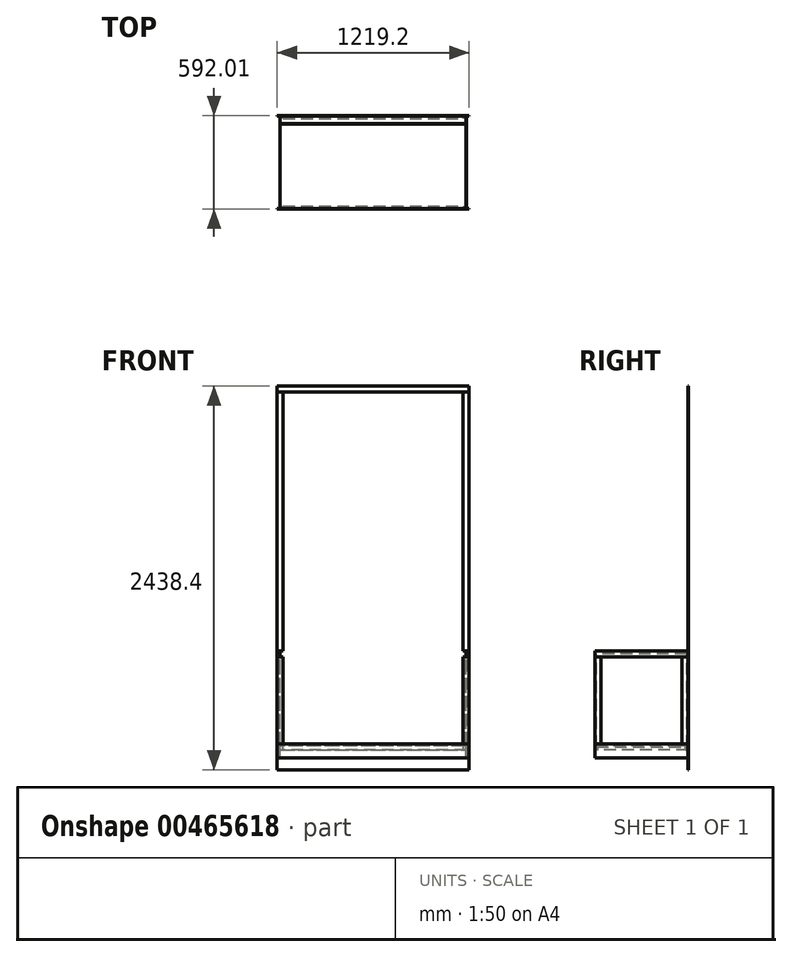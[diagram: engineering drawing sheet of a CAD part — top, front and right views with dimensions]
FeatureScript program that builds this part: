
annotation { "Feature Type Name" : "Feature", "Feature Type Description" : "" }
export const myFeature = defineFeature(function(context is Context, id is Id, definition is map)
    precondition{}
    {
        {
            assignVariable(context, id + "F0", {"name" : "TotalHeight", "anyValue" : 24});
        }
        {
            assignVariable(context, id + "F1", {"name" : "x1", "anyValue" : 0.75});
        }
        {
            assignVariable(context, id + "F2", {"name" : "PlyThk", "anyValue" : 23 / 32});
        }
        {
            var Q0;
            Q0=qCreatedBy(makeId("Top.planeOp"),FACE);
            var sketch = newSketch(context, id + "F3", { "sketchPlane" : qUnion([Q0])});
            skLineSegment(sketch, "E0.bottom", {"start": v(609.6, 295.28) * mm, "end": v(-609.6, 295.27) * mm, "construction": true});
            skLineSegment(sketch, "E0.top", {"start": v(609.6, -314.32) * mm, "end": v(-609.6, -314.33) * mm, "construction": true});
            skLineSegment(sketch, "E0.left", {"start": v(609.6, 295.28) * mm, "end": v(609.6, -314.32) * mm, "construction": true});
            skLineSegment(sketch, "E0.right", {"start": v(-609.6, 295.27) * mm, "end": v(-609.6, -314.33) * mm, "construction": true});
            skPoint(sketch, "E0.middle", {"position": v(0, 0) * mm});
            skLineSegment(sketch, "E1.bottom", {"start": v(590.55, 295.28) * mm, "end": v(-590.55, 295.27) * mm});
            skLineSegment(sketch, "E1.top", {"start": v(590.55, -295.27) * mm, "end": v(-590.55, -295.28) * mm});
            skLineSegment(sketch, "E1.left", {"start": v(590.55, 295.28) * mm, "end": v(590.55, -295.27) * mm});
            skLineSegment(sketch, "E1.right", {"start": v(-590.55, 295.27) * mm, "end": v(-590.55, -295.28) * mm});
            skSolve(sketch);
        }
        {
            var Q0;
            Q0=makeQuery(id+"F3.imprint","IMPRINT",FACE,{"disambiguationData":[TD([[makeQuery(id+"F3.imprint","IMPRINT",EDGE,{"derivedFrom":sQuery(id+"F3.wireOp",EDGE,"E1.bottom")}),1.0]])]});
            extrude(context, id + "F4", {"entities" : qUnion([Q0]), "depth" : (getVariable(context, 'PlyThk')) * mm});
        }
        {
            var Q0;
            Q0=makeQuery(id+"F4.opExtrude","CAP_FACE",FACE,{"disambiguationData":[OSD([sQuery(id+"F3.wireOp",EDGE,"E1.bottom"),sQuery(id+"F3.wireOp",EDGE,"E1.top"),sQuery(id+"F3.wireOp",EDGE,"E1.left"),sQuery(id+"F3.wireOp",EDGE,"E1.right")])],"isStart":true});
            cPlane(context, id + "F5", {"entities" : qUnion([Q0]), "cplaneType" : CPlaneType.OFFSET, "offset" : (getVariable(context, 'TotalHeight')) * mm, "oppositeDirection" : true, "width" : 152.4 * mm, "height" : 152.4 * mm});
        }
        {
            var Q0;
            Q0=qCreatedBy(id+"F5.planeOp",FACE);
            var sketch = newSketch(context, id + "F6", { "sketchPlane" : qUnion([Q0])});
            skLineSegment(sketch, "E2.0", {"start": v(590.55, 295.27) * mm, "end": v(-590.55, 295.28) * mm});
            skLineSegment(sketch, "E3", {"start": v(-590.55, 295.28) * mm, "end": v(-590.55, 286.15) * mm});
            skLineSegment(sketch, "E4", {"start": v(-590.55, 286.15) * mm, "end": v(-572.3, 286.15) * mm});
            skLineSegment(sketch, "E5", {"start": v(-572.3, 286.15) * mm, "end": v(-572.3, 277.02) * mm});
            skLineSegment(sketch, "E6.MirrorCS", {"start": v(590.55, 295.28) * mm, "end": v(590.55, 286.15) * mm});
            skLineSegment(sketch, "E7.MirrorCS", {"start": v(572.3, 286.15) * mm, "end": v(572.3, 277.02) * mm});
            skLineSegment(sketch, "E8.MirrorCS", {"start": v(590.55, 286.15) * mm, "end": v(572.3, 286.15) * mm});
            skLineSegment(sketch, "E9", {"start": v(572.3, 277.02) * mm, "end": v(-572.3, 277.02) * mm});
            skLineSegment(sketch, "E10.MirrorCS", {"start": v(-590.55, -295.28) * mm, "end": v(-590.55, -286.15) * mm});
            skLineSegment(sketch, "E11.MirrorCS", {"start": v(-590.55, -286.15) * mm, "end": v(-572.3, -286.15) * mm});
            skLineSegment(sketch, "E12.MirrorCS", {"start": v(-572.3, -286.15) * mm, "end": v(-572.3, -277.02) * mm});
            skLineSegment(sketch, "E13.MirrorCS", {"start": v(590.55, -295.28) * mm, "end": v(590.55, -286.15) * mm});
            skLineSegment(sketch, "E14.MirrorCS", {"start": v(572.3, -286.15) * mm, "end": v(572.3, -277.02) * mm});
            skLineSegment(sketch, "E15.MirrorCS", {"start": v(590.55, -286.15) * mm, "end": v(572.3, -286.15) * mm});
            skLineSegment(sketch, "E16.MirrorCS", {"start": v(590.55, -295.27) * mm, "end": v(-590.55, -295.27) * mm});
            skLineSegment(sketch, "E17.MirrorCS", {"start": v(572.3, -277.02) * mm, "end": v(-572.3, -277.02) * mm});
            skSolve(sketch);
        }
        {
            var Q0;
            Q0=makeQuery(id+"F6.imprint","IMPRINT",FACE,{"disambiguationData":[TD([[makeQuery(id+"F6.imprint","IMPRINT",EDGE,{"derivedFrom":sQuery(id+"F6.wireOp",EDGE,"E2.0")}),1.0]])]});
            var Q1;
            Q1=makeQuery(id+"F6.imprint","IMPRINT",FACE,{"disambiguationData":[TD([[makeQuery(id+"F6.imprint","IMPRINT",EDGE,{"derivedFrom":sQuery(id+"F6.wireOp",EDGE,"E10.MirrorCS")}),-1.0]])]});
            var Q2;
            Q2=makeQuery(id+"F4.opExtrude","CAP_FACE",FACE,{"disambiguationData":[OSD([sQuery(id+"F3.wireOp",EDGE,"E1.bottom"),sQuery(id+"F3.wireOp",EDGE,"E1.top"),sQuery(id+"F3.wireOp",EDGE,"E1.left"),sQuery(id+"F3.wireOp",EDGE,"E1.right")])],"isStart":false});
            extrude(context, id + "F7", {"entities" : qUnion([Q0, Q1]), "endBound" : BoundingType.UP_TO_SURFACE, "endBoundEntityFace" : qUnion([Q2]), "depth" : 25.4 * mm});
        }
        {
            var Q0;
            Q0=makeQuery(id+"F7.opExtrude","SWEPT_FACE",FACE,{"disambiguationData":[OSD([sQuery(id+"F6.wireOp",EDGE,"E6.MirrorCS")])]});
            var sketch = newSketch(context, id + "F8", { "sketchPlane" : qUnion([Q0])});
            skLineSegment(sketch, "E18.0", {"start": v(-286.15, 18.26) * mm, "end": v(-286.15, 609.6) * mm});
            skLineSegment(sketch, "E19.0", {"start": v(286.15, 18.26) * mm, "end": v(286.15, 609.6) * mm});
            skLineSegment(sketch, "E20", {"start": v(286.15, 609.6) * mm, "end": v(-286.15, 609.6) * mm});
            skLineSegment(sketch, "E21", {"start": v(-286.15, 18.26) * mm, "end": v(286.15, 18.26) * mm});
            skSolve(sketch);
        }
        {
            var Q0;
            Q0 = qSketchRegion(id + "F8", true);
            extrude(context, id + "F9", {"entities" : qUnion([Q0]), "oppositeDirection" : true, "depth" : (getVariable(context, 'PlyThk')) * mm});
        }
        {
            var Q0;
            Q0=makeQuery(id+"F9.opExtrude","SWEPT_BODY",BODY,{"disambiguationData":[OSD([sQuery(id+"F8.wireOp",EDGE,"E18.0"),sQuery(id+"F8.wireOp",EDGE,"E19.0"),sQuery(id+"F8.wireOp",EDGE,"E20"),sQuery(id+"F8.wireOp",EDGE,"E21")])]});
            var Q1;
            Q1=qCreatedBy(makeId("Right.planeOp"),FACE);
            mirror(context, id + "F10", {"entities" : qUnion([Q0]), "mirrorPlane" : qUnion([Q1])});
        }
        {
            var Q0;
            Q0=makeQuery(id+"F10.opPattern","COPY",FACE,{"derivedFrom":makeQuery(id+"F9.opExtrude","CAP_FACE",FACE,{"disambiguationData":[OSD([sQuery(id+"F8.wireOp",EDGE,"E18.0"),sQuery(id+"F8.wireOp",EDGE,"E19.0"),sQuery(id+"F8.wireOp",EDGE,"E20"),sQuery(id+"F8.wireOp",EDGE,"E21")])],"isStart":true}),"instanceName":"1"});
            var sketch = newSketch(context, id + "F11", { "sketchPlane" : qUnion([Q0])});
            skPoint(sketch, "E22.0", {"position": v(290.71, 609.6) * mm});
            skLineSegment(sketch, "E23.0", {"start": v(295.27, 609.6) * mm, "end": v(286.15, 609.6) * mm});
            skLineSegment(sketch, "E24.0", {"start": v(-295.27, 609.6) * mm, "end": v(-286.15, 609.6) * mm});
            skLineSegment(sketch, "E25.0", {"start": v(-295.28, 18.26) * mm, "end": v(-295.28, 609.6) * mm});
            skLineSegment(sketch, "E26.0", {"start": v(295.28, 18.26) * mm, "end": v(295.28, 609.6) * mm});
            skLineSegment(sketch, "E27", {"start": v(295.28, 589.76) * mm, "end": v(-295.28, 589.76) * mm});
            skLineSegment(sketch, "E28.bottom", {"start": v(-295.27, 38.1) * mm, "end": v(295.27, 38.1) * mm});
            skLineSegment(sketch, "E28.top", {"start": v(-295.27, -50.8) * mm, "end": v(295.27, -50.8) * mm});
            skLineSegment(sketch, "E28.left", {"start": v(-295.27, 38.1) * mm, "end": v(-295.27, -50.8) * mm});
            skLineSegment(sketch, "E28.right", {"start": v(295.27, 38.1) * mm, "end": v(295.27, -50.8) * mm});
            skLineSegment(sketch, "E29", {"start": v(-257.17, 589.76) * mm, "end": v(-257.17, 38.1) * mm});
            skLineSegment(sketch, "E30", {"start": v(257.17, 589.76) * mm, "end": v(257.18, 38.1) * mm});
            skLineSegment(sketch, "E31", {"start": v(-295.27, 609.6) * mm, "end": v(-295.27, 627.86) * mm});
            skLineSegment(sketch, "E32", {"start": v(-295.28, 627.86) * mm, "end": v(295.28, 627.86) * mm});
            skLineSegment(sketch, "E33", {"start": v(295.27, 627.86) * mm, "end": v(295.27, 609.6) * mm});
            skSolve(sketch);
        }
        {
            var Q0;
            {var subQ0=sQuery(id+"F11.wireOp",EDGE,"E23.0");Q0=makeQuery(id+"F11.imprint","IMPRINT",FACE,{"disambiguationData":[TD([[makeQuery(id+"F11.imprint","IMPRINT",EDGE,{"derivedFrom":subQ0}),1.0]])]});}
            var Q1;
            {var subQ0=sQuery(id+"F11.wireOp",EDGE,"E24.0");Q1=makeQuery(id+"F11.imprint","IMPRINT",FACE,{"disambiguationData":[TD([[makeQuery(id+"F11.imprint","IMPRINT",EDGE,{"derivedFrom":subQ0}),-1.0]])]});}
            var Q2;
            {var subQ3=sQuery(id+"F11.wireOp",EDGE,"E28.top");Q2=makeQuery(id+"F11.imprint","IMPRINT",FACE,{"disambiguationData":[TD([[makeQuery(id+"F11.imprint","IMPRINT",EDGE,{"derivedFrom":subQ3}),1.0]])]});}
            var Q3;
            {var subQ0=makeQuery(id+"F10.opPattern","COPY",EDGE,{"derivedFrom":makeQuery(id+"F9.opExtrude","CAP_EDGE",EDGE,{"disambiguationData":[OSD([sQuery(id+"F8.wireOp",EDGE,"E21")])],"isStart":true}),"instanceName":"1"});Q3=makeQuery(id+"F11.imprint","IMPRINT",FACE,{"disambiguationData":[TD([[makeQuery(id+"F11.imprint","IMPRINT",EDGE,{"derivedFrom":subQ0}),-1.0]])]});}
            var Q4;
            {var subQ7=sQuery(id+"F11.wireOp",EDGE,"92d246fa-3d92-4376-9fad-c65cf3820cd6.0");Q4=makeQuery(id+"F11.imprint","IMPRINT",FACE,{"disambiguationData":[TD([[makeQuery(id+"F11.imprint","IMPRINT",EDGE,{"derivedFrom":subQ7}),-1.0]])]});}
            var Q5;
            Q5=makeQuery(id+"F11.imprint","IMPRINT",FACE,{"disambiguationData":[TD([[makeQuery(id+"F11.imprint","IMPRINT",EDGE,{"derivedFrom":sQuery(id+"F11.wireOp",EDGE,"E23.0")}),-1.0]])]});
            var Q6;
            {var subQ0=makeQuery(id+"F10.opPattern","COPY",EDGE,{"derivedFrom":makeQuery(id+"F9.opExtrude","CAP_EDGE",EDGE,{"disambiguationData":[OSD([sQuery(id+"F8.wireOp",EDGE,"E20")])],"isStart":true}),"instanceName":"1"});Q6=makeQuery(id+"F11.imprint","IMPRINT",FACE,{"disambiguationData":[TD([[makeQuery(id+"F11.imprint","IMPRINT",EDGE,{"derivedFrom":subQ0}),-1.0]])]});}
            extrude(context, id + "F12", {"entities" : qUnion([Q0, Q1, Q2, Q3, Q4, Q5, Q6]), "depth" : (getVariable(context, 'x1')) * mm});
        }
        {
            var Q0;
            {var subQ0=sQuery(id+"F11.wireOp",EDGE,"E29");Q0=makeQuery(id+"F11.imprint","IMPRINT",FACE,{"disambiguationData":[TD([[makeQuery(id+"F11.imprint","IMPRINT",EDGE,{"derivedFrom":subQ0}),-1.0]])]});}
            var Q1;
            {var subQ1=sQuery(id+"F11.wireOp",EDGE,"E25.0");var subQ3=sQuery(id+"F11.wireOp",EDGE,"E27");var subQ4=makeQuery(id+"F11.imprint","INTERSECT",VERTEX,{"derivedFrom":[subQ1,subQ3]});Q1=makeQuery(id+"F11.imprint","IMPRINT",FACE,{"disambiguationData":[TD([[makeQuery(id+"F11.imprint","IMPRINT",EDGE,{"disambiguationData":[TD([[subQ4,1.0]])],"derivedFrom":subQ3}),1.0]])]});}
            var Q2;
            {var subQ0=sQuery(id+"F11.wireOp",EDGE,"E30");Q2=makeQuery(id+"F11.imprint","IMPRINT",FACE,{"disambiguationData":[TD([[makeQuery(id+"F11.imprint","IMPRINT",EDGE,{"derivedFrom":subQ0}),1.0]])]});}
            var Q3;
            {var subQ1=sQuery(id+"F11.wireOp",EDGE,"E26.0");var subQ3=sQuery(id+"F11.wireOp",EDGE,"E27");var subQ4=makeQuery(id+"F11.imprint","INTERSECT",VERTEX,{"derivedFrom":[subQ1,subQ3]});Q3=makeQuery(id+"F11.imprint","IMPRINT",FACE,{"disambiguationData":[TD([[makeQuery(id+"F11.imprint","IMPRINT",EDGE,{"disambiguationData":[TD([[subQ4,-1.0]])],"derivedFrom":subQ3}),1.0]])]});}
            extrude(context, id + "F13", {"entities" : qUnion([Q0, Q1, Q2, Q3]), "depth" : (getVariable(context, 'x1')) * mm});
        }
        {
            var Q0;
            Q0=makeQuery(id+"F12.opExtrude","SWEPT_BODY",BODY,{"disambiguationData":[OSD([sQuery(id+"F11.wireOp",EDGE,"E28.bottom"),sQuery(id+"F11.wireOp",EDGE,"E28.top"),sQuery(id+"F11.wireOp",EDGE,"E28.left"),sQuery(id+"F11.wireOp",EDGE,"E28.right")])]});
            var Q1;
            Q1=makeQuery(id+"F13.opExtrude","SWEPT_BODY",BODY,{"disambiguationData":[OSD([sQuery(id+"F11.wireOp",EDGE,"E26.0"),sQuery(id+"F11.wireOp",EDGE,"E27"),sQuery(id+"F11.wireOp",EDGE,"E28.bottom"),sQuery(id+"F11.wireOp",EDGE,"E30")])]});
            var Q2;
            Q2=makeQuery(id+"F12.opExtrude","SWEPT_BODY",BODY,{"disambiguationData":[OSD([sQuery(id+"F11.wireOp",EDGE,"92d246fa-3d92-4376-9fad-c65cf3820cd6.0"),sQuery(id+"F11.wireOp",EDGE,"E23.0"),sQuery(id+"F11.wireOp",EDGE,"E24.0"),sQuery(id+"F11.wireOp",EDGE,"E25.0"),sQuery(id+"F11.wireOp",EDGE,"E26.0"),sQuery(id+"F11.wireOp",EDGE,"E27")])]});
            var Q3;
            Q3=makeQuery(id+"F13.opExtrude","SWEPT_BODY",BODY,{"disambiguationData":[OSD([sQuery(id+"F11.wireOp",EDGE,"E25.0"),sQuery(id+"F11.wireOp",EDGE,"E27"),sQuery(id+"F11.wireOp",EDGE,"E28.bottom"),sQuery(id+"F11.wireOp",EDGE,"E29")])]});
            var Q4;
            Q4=qCreatedBy(makeId("Right.planeOp"),FACE);
            mirror(context, id + "F14", {"entities" : qUnion([Q0, Q1, Q2, Q3]), "mirrorPlane" : qUnion([Q4])});
        }
        {
            var Q0;
            Q0=makeQuery(id+"F7.opExtrude","SWEPT_FACE",FACE,{"disambiguationData":[OSD([sQuery(id+"F6.wireOp",EDGE,"E2.0")])]});
            var sketch = newSketch(context, id + "F15", { "sketchPlane" : qUnion([Q0])});
            skLineSegment(sketch, "E34.0", {"start": v(-609.6, 38.1) * mm, "end": v(-609.6, 589.76) * mm});
            skLineSegment(sketch, "E35.0", {"start": v(-609.6, 589.76) * mm, "end": v(-609.6, 589.76) * mm});
            skLineSegment(sketch, "E36.0", {"start": v(-609.6, 38.1) * mm, "end": v(-609.6, -50.8) * mm});
            skLineSegment(sketch, "E37.0", {"start": v(609.6, 38.1) * mm, "end": v(609.6, -50.8) * mm});
            skLineSegment(sketch, "E38", {"start": v(609.6, -50.8) * mm, "end": v(-609.6, -50.8) * mm});
            skLineSegment(sketch, "E39", {"start": v(-609.6, 38.1) * mm, "end": v(609.6, 38.1) * mm});
            skLineSegment(sketch, "E40", {"start": v(-609.6, 589.76) * mm, "end": v(609.6, 589.76) * mm});
            skLineSegment(sketch, "E41.0", {"start": v(609.6, 589.76) * mm, "end": v(609.6, 589.76) * mm});
            skLineSegment(sketch, "E42.0.0", {"start": v(590.55, 589.76) * mm, "end": v(590.55, 589.76) * mm});
            skLineSegment(sketch, "E42.0.1", {"start": v(590.55, 589.76) * mm, "end": v(609.6, 589.76) * mm});
            skLineSegment(sketch, "E42.0.3", {"start": v(590.55, 589.76) * mm, "end": v(609.6, 589.76) * mm});
            skLineSegment(sketch, "E43.0.0", {"start": v(-590.55, 589.76) * mm, "end": v(-590.55, 589.76) * mm});
            skLineSegment(sketch, "E43.0.1", {"start": v(-609.6, 589.76) * mm, "end": v(-590.55, 589.76) * mm});
            skLineSegment(sketch, "E43.0.3", {"start": v(-609.6, 589.76) * mm, "end": v(-590.55, 589.76) * mm});
            skLineSegment(sketch, "E44", {"start": v(-571.5, 589.76) * mm, "end": v(-571.5, 38.1) * mm});
            skLineSegment(sketch, "E45", {"start": v(571.5, 589.76) * mm, "end": v(571.5, 38.1) * mm});
            skLineSegment(sketch, "E46", {"start": v(609.6, 589.76) * mm, "end": v(609.6, 38.1) * mm});
            skLineSegment(sketch, "E47", {"start": v(590.55, 627.86) * mm, "end": v(-590.55, 627.86) * mm});
            skLineSegment(sketch, "E48", {"start": v(609.6, 589.76) * mm, "end": v(609.6, 627.86) * mm});
            skLineSegment(sketch, "E49", {"start": v(609.6, 627.86) * mm, "end": v(590.55, 627.86) * mm});
            skLineSegment(sketch, "E50", {"start": v(-609.6, 589.76) * mm, "end": v(-609.6, 627.86) * mm});
            skLineSegment(sketch, "E51", {"start": v(-609.6, 627.86) * mm, "end": v(-590.55, 627.86) * mm});
            skSolve(sketch);
        }
        {
            var Q0;
            {var subQ1=sQuery(id+"F15.wireOp",EDGE,"E36.0");Q0=makeQuery(id+"F15.imprint","IMPRINT",FACE,{"disambiguationData":[TD([[makeQuery(id+"F15.imprint","IMPRINT",EDGE,{"derivedFrom":subQ1}),1.0]])]});}
            var Q1;
            {var subQ2=sQuery(id+"F15.wireOp",EDGE,"E39");var subQ6=makeQuery(id+"F15.imprint","INTERSECT",VERTEX,{"derivedFrom":[subQ2,sQuery(id+"F15.wireOp",EDGE,"E44")]});Q1=makeQuery(id+"F15.imprint","IMPRINT",FACE,{"disambiguationData":[TD([[makeQuery(id+"F15.imprint","IMPRINT",EDGE,{"disambiguationData":[TD([[subQ6,-1.0]])],"derivedFrom":subQ2}),-1.0]])]});}
            var Q2;
            {var subQ0=sQuery(id+"F15.wireOp",EDGE,"E42.0.0");Q2=makeQuery(id+"F15.imprint","IMPRINT",FACE,{"disambiguationData":[TD([[makeQuery(id+"F15.imprint","IMPRINT",EDGE,{"derivedFrom":subQ0}),1.0]])]});}
            var Q3;
            Q3=makeQuery(id+"F15.imprint","IMPRINT",FACE,{"disambiguationData":[TD([[makeQuery(id+"F15.imprint","IMPRINT",EDGE,{"derivedFrom":sQuery(id+"F15.wireOp",EDGE,"E43.0.0")}),1.0]])]});
            var Q4;
            Q4=makeQuery(id+"F15.imprint","IMPRINT",FACE,{"disambiguationData":[TD([[makeQuery(id+"F15.imprint","IMPRINT",EDGE,{"derivedFrom":sQuery(id+"F15.wireOp",EDGE,"E42.0.0")}),-1.0]])]});
            var Q5;
            {var subQ4=sQuery(id+"F15.wireOp",EDGE,"E42.0.3");Q5=makeQuery(id+"F15.imprint","IMPRINT",FACE,{"disambiguationData":[TD([[makeQuery(id+"F15.imprint","IMPRINT",EDGE,{"derivedFrom":subQ4}),1.0]])]});}
            var Q6;
            {var subQ0=sQuery(id+"F6.wireOp",EDGE,"E2.0");var subQ1=makeQuery(id+"F7.opExtrude","CAP_EDGE",EDGE,{"disambiguationData":[OSD([subQ0])],"isStart":true});Q6=makeQuery(id+"F15.imprint","IMPRINT",FACE,{"disambiguationData":[TD([[makeQuery(id+"F15.imprint","IMPRINT",EDGE,{"derivedFrom":subQ1}),1.0]])]});}
            extrude(context, id + "F16", {"entities" : qUnion([Q0, Q1, Q2, Q3, Q4, Q5, Q6]), "depth" : (getVariable(context, 'x1')) * mm});
        }
        {
            var Q0;
            {var subQ0=sQuery(id+"F15.wireOp",EDGE,"E44");Q0=makeQuery(id+"F15.imprint","IMPRINT",FACE,{"disambiguationData":[TD([[makeQuery(id+"F15.imprint","IMPRINT",EDGE,{"derivedFrom":subQ0}),-1.0]])]});}
            var Q1;
            {var subQ0=sQuery(id+"F15.wireOp",EDGE,"E34.0");Q1=makeQuery(id+"F15.imprint","IMPRINT",FACE,{"disambiguationData":[TD([[makeQuery(id+"F15.imprint","IMPRINT",EDGE,{"derivedFrom":subQ0}),-1.0]])]});}
            var Q2;
            {var subQ4=sQuery(id+"F15.wireOp",EDGE,"E42.0.1");Q2=makeQuery(id+"F15.imprint","IMPRINT",FACE,{"disambiguationData":[TD([[makeQuery(id+"F15.imprint","IMPRINT",EDGE,{"derivedFrom":subQ4}),-1.0]])]});}
            var Q3;
            {var subQ4=sQuery(id+"F15.wireOp",EDGE,"E42.0.3");Q3=makeQuery(id+"F15.imprint","IMPRINT",FACE,{"disambiguationData":[TD([[makeQuery(id+"F15.imprint","IMPRINT",EDGE,{"derivedFrom":subQ4}),-1.0]])]});}
            var Q4;
            {var subQ0=sQuery(id+"F15.wireOp",EDGE,"E45");Q4=makeQuery(id+"F15.imprint","IMPRINT",FACE,{"disambiguationData":[TD([[makeQuery(id+"F15.imprint","IMPRINT",EDGE,{"derivedFrom":subQ0}),1.0]])]});}
            extrude(context, id + "F17", {"entities" : qUnion([Q0, Q1, Q2, Q3, Q4]), "depth" : (getVariable(context, 'x1')) * mm});
        }
        {
            var Q0;
            Q0=qCreatedBy(id+"F5.planeOp",FACE);
            var sketch = newSketch(context, id + "F18", { "sketchPlane" : qUnion([Q0])});
            skLineSegment(sketch, "E52.0", {"start": v(590.55, -295.27) * mm, "end": v(-590.55, -295.27) * mm});
            skLineSegment(sketch, "E53.0", {"start": v(-609.6, 295.28) * mm, "end": v(609.6, 295.27) * mm});
            skLineSegment(sketch, "E54", {"start": v(590.55, -244.47) * mm, "end": v(-590.55, -244.47) * mm});
            skLineSegment(sketch, "E55", {"start": v(-590.55, -241.3) * mm, "end": v(590.55, -241.3) * mm});
            skLineSegment(sketch, "E56.0", {"start": v(-590.55, -295.27) * mm, "end": v(-590.55, 295.28) * mm});
            skLineSegment(sketch, "E57.0", {"start": v(590.55, -295.27) * mm, "end": v(590.55, 295.28) * mm});
            skLineSegment(sketch, "E58.0", {"start": v(-609.6, 314.33) * mm, "end": v(-609.6, 295.28) * mm, "construction": true});
            skSolve(sketch);
        }
        {
            var Q0;
            {var subQ3=sQuery(id+"F18.wireOp",EDGE,"E55");Q0=makeQuery(id+"F18.imprint","IMPRINT",FACE,{"disambiguationData":[TD([[makeQuery(id+"F18.imprint","IMPRINT",EDGE,{"derivedFrom":subQ3}),1.0]])]});}
            extrude(context, id + "F19", {"entities" : qUnion([Q0]), "oppositeDirection" : true, "depth" : (getVariable(context, 'PlyThk')) * mm});
        }
        {
            var Q0;
            {var subQ0=sQuery(id+"F18.wireOp",EDGE,"E52.0");Q0=makeQuery(id+"F18.imprint","IMPRINT",FACE,{"disambiguationData":[TD([[makeQuery(id+"F18.imprint","IMPRINT",EDGE,{"derivedFrom":subQ0}),-1.0]])]});}
            extrude(context, id + "F20", {"entities" : qUnion([Q0]), "oppositeDirection" : true, "depth" : (getVariable(context, 'PlyThk')) * mm});
        }
        {
            var Q0;
            Q0=makeQuery(id+"F7.opExtrude","SWEPT_FACE",FACE,{"disambiguationData":[OSD([sQuery(id+"F6.wireOp",EDGE,"E16.MirrorCS")])]});
            var sketch = newSketch(context, id + "F21", { "sketchPlane" : qUnion([Q0])});
            skPoint(sketch, "E59.0", {"position": v(-609.6, -50.8) * mm});
            skLineSegment(sketch, "E60.0", {"start": v(609.6, 589.76) * mm, "end": v(609.6, 627.86) * mm, "construction": true});
            skLineSegment(sketch, "E61.bottom", {"start": v(-609.6, -127) * mm, "end": v(609.6, -127) * mm});
            skLineSegment(sketch, "E61.top", {"start": v(-609.6, 2311.4) * mm, "end": v(609.6, 2311.4) * mm});
            skLineSegment(sketch, "E61.left", {"start": v(-609.6, -127) * mm, "end": v(-609.6, 2311.4) * mm});
            skLineSegment(sketch, "E61.right", {"start": v(609.6, -127) * mm, "end": v(609.6, 2311.4) * mm});
            skSolve(sketch);
        }
        {
            var Q0;
            Q0 = qSketchRegion(id + "F21", true);
            extrude(context, id + "F22", {"entities" : qUnion([Q0]), "depth" : (getVariable(context, 'PlyThk')) * mm});
        }
        {
            var Q0;
            Q0=makeQuery(id+"F22.opExtrude","CAP_FACE",FACE,{"disambiguationData":[OSD([sQuery(id+"F21.wireOp",EDGE,"E61.bottom"),sQuery(id+"F21.wireOp",EDGE,"E61.top"),sQuery(id+"F21.wireOp",EDGE,"E61.left"),sQuery(id+"F21.wireOp",EDGE,"E61.right")])],"isStart":true});
            var sketch = newSketch(context, id + "F23", { "sketchPlane" : qUnion([Q0])});
            skLineSegment(sketch, "E62.0.0", {"start": v(609.6, 2311.4) * mm, "end": v(-609.6, 2311.4) * mm});
            skLineSegment(sketch, "E62.0.1", {"start": v(-609.6, 2311.4) * mm, "end": v(-609.6, -127) * mm});
            skLineSegment(sketch, "E62.0.2", {"start": v(-609.6, -127) * mm, "end": v(609.6, -127) * mm});
            skLineSegment(sketch, "E62.0.3", {"start": v(609.6, -127) * mm, "end": v(609.6, 2311.4) * mm});
            skLineSegment(sketch, "E63.0", {"start": v(-609.6, 627.86) * mm, "end": v(-590.55, 627.86) * mm});
            skLineSegment(sketch, "E64.0", {"start": v(609.6, 627.86) * mm, "end": v(590.55, 627.86) * mm});
            skLineSegment(sketch, "E65", {"start": v(-609.6, 2273.3) * mm, "end": v(609.6, 2273.3) * mm});
            skLineSegment(sketch, "E66.0", {"start": v(590.55, 627.86) * mm, "end": v(590.55, 627.86) * mm});
            skLineSegment(sketch, "E67", {"start": v(571.5, 627.86) * mm, "end": v(571.5, 2273.3) * mm});
            skLineSegment(sketch, "E68", {"start": v(-571.5, 2273.3) * mm, "end": v(-571.5, 627.86) * mm});
            skLineSegment(sketch, "E69", {"start": v(-590.55, 627.86) * mm, "end": v(-571.5, 627.86) * mm});
            skLineSegment(sketch, "E70", {"start": v(590.55, 627.86) * mm, "end": v(571.5, 627.86) * mm});
            skSolve(sketch);
        }
        {
            var Q0;
            {var subQ1=sQuery(id+"F23.wireOp",EDGE,"E62.0.0");Q0=makeQuery(id+"F23.imprint","IMPRINT",FACE,{"disambiguationData":[TD([[makeQuery(id+"F23.imprint","IMPRINT",EDGE,{"derivedFrom":subQ1}),1.0]])]});}
            extrude(context, id + "F24", {"entities" : qUnion([Q0]), "depth" : (getVariable(context, 'x1')) * mm});
        }
        {
            var Q0;
            {var subQ1=sQuery(id+"F23.wireOp",EDGE,"E63.0");Q0=makeQuery(id+"F23.imprint","IMPRINT",FACE,{"disambiguationData":[TD([[makeQuery(id+"F23.imprint","IMPRINT",EDGE,{"derivedFrom":subQ1}),1.0]])]});}
            var Q1;
            {var subQ1=sQuery(id+"F23.wireOp",EDGE,"E64.0");Q1=makeQuery(id+"F23.imprint","IMPRINT",FACE,{"disambiguationData":[TD([[makeQuery(id+"F23.imprint","IMPRINT",EDGE,{"derivedFrom":subQ1}),-1.0]])]});}
            extrude(context, id + "F25", {"entities" : qUnion([Q0, Q1]), "depth" : (getVariable(context, 'x1')) * mm});
        }
    });
